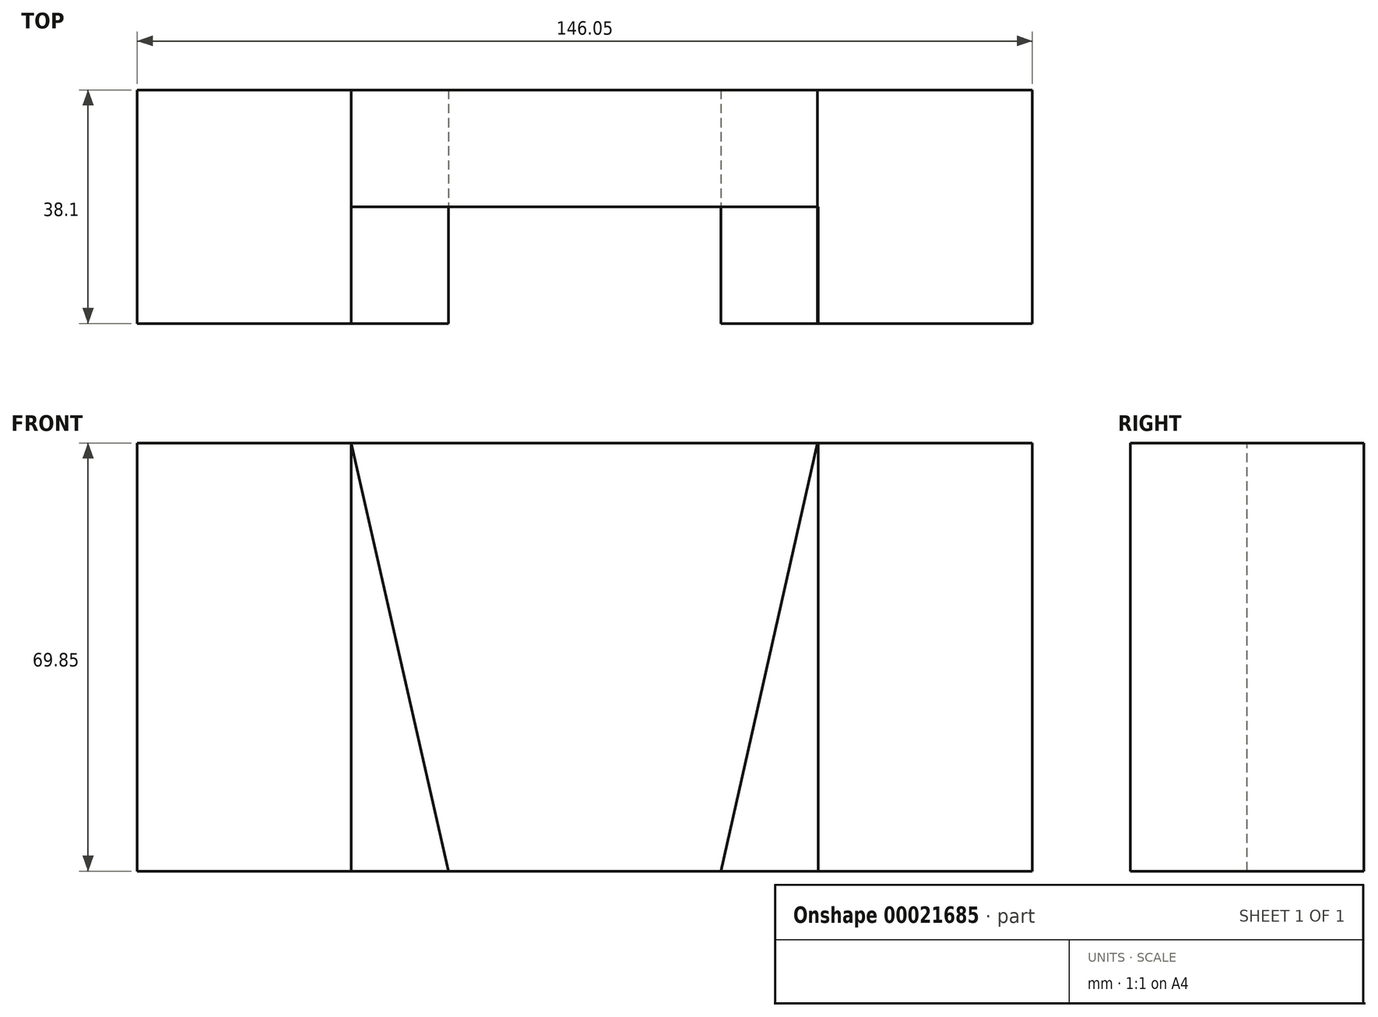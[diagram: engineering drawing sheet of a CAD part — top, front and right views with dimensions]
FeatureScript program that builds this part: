
annotation { "Feature Type Name" : "Feature", "Feature Type Description" : "" }
export const myFeature = defineFeature(function(context is Context, id is Id, definition is map)
    precondition{}
    {
        {
            var Q0;
            Q0=qCreatedBy(makeId("Top.planeOp"),FACE);
            var sketch = newSketch(context, id + "F0", { "sketchPlane" : qUnion([Q0])});
            skLineSegment(sketch, "E0", {"start": v(-74.2, 38.1) * mm, "end": v(71.85, 38.1) * mm});
            skLineSegment(sketch, "E1", {"start": v(-74.2, 38.1) * mm, "end": v(-74.2, 0) * mm});
            skLineSegment(sketch, "E2", {"start": v(71.85, 38.1) * mm, "end": v(36.92, 38.1) * mm});
            skLineSegment(sketch, "E3", {"start": v(36.92, 38.1) * mm, "end": v(-39.28, 38.1) * mm});
            skLineSegment(sketch, "E4", {"start": v(-74.2, 0) * mm, "end": v(-39.28, 0) * mm});
            skLineSegment(sketch, "E5", {"start": v(-39.28, 0) * mm, "end": v(-39.28, 19.05) * mm});
            skLineSegment(sketch, "E6", {"start": v(-39.28, 19.05) * mm, "end": v(36.92, 19.05) * mm});
            skLineSegment(sketch, "E7", {"start": v(36.92, 19.05) * mm, "end": v(36.92, 0) * mm});
            skLineSegment(sketch, "E8", {"start": v(36.92, 0) * mm, "end": v(71.85, 0) * mm});
            skLineSegment(sketch, "E9", {"start": v(71.85, 0) * mm, "end": v(71.85, 38.1) * mm});
            skSolve(sketch);
        }
        {
            var Q0;
            Q0=qCreatedBy(makeId("Front.planeOp"),FACE);
            var sketch = newSketch(context, id + "F1", { "sketchPlane" : qUnion([Q0])});
            skLineSegment(sketch, "E10", {"start": v(-74.2, 0) * mm, "end": v(-74.2, -69.85) * mm});
            skLineSegment(sketch, "E11", {"start": v(-74.2, -69.85) * mm, "end": v(-23.4, -69.85) * mm});
            skLineSegment(sketch, "E12", {"start": v(-23.4, -69.85) * mm, "end": v(-39.28, 0) * mm});
            skLineSegment(sketch, "E13", {"start": v(71.85, 0) * mm, "end": v(71.85, -69.85) * mm});
            skLineSegment(sketch, "E14", {"start": v(71.85, -69.85) * mm, "end": v(21.05, -69.85) * mm});
            skLineSegment(sketch, "E15", {"start": v(21.05, -69.85) * mm, "end": v(36.8, 0) * mm});
            skLineSegment(sketch, "E16", {"start": v(-74.2, 0) * mm, "end": v(-39.28, 0) * mm});
            skLineSegment(sketch, "E17", {"start": v(36.8, 0) * mm, "end": v(71.85, 0) * mm});
            skSolve(sketch);
        }
        {
            var Q0;
            Q0=makeQuery(id+"F1.imprint","IMPRINT",FACE,{"disambiguationData":[TD([[makeQuery(id+"F1.imprint","IMPRINT",EDGE,{"derivedFrom":sQuery(id+"F1.wireOp",EDGE,"E10")}),1.0]])]});
            var Q1;
            Q1=makeQuery(id+"F1.imprint","IMPRINT",FACE,{"disambiguationData":[TD([[makeQuery(id+"F1.imprint","IMPRINT",EDGE,{"derivedFrom":sQuery(id+"F1.wireOp",EDGE,"E13")}),-1.0]])]});
            extrude(context, id + "F2", {"entities" : qUnion([Q0, Q1]), "oppositeDirection" : true, "depth" : 38.1 * mm});
        }
        {
            var Q0;
            Q0=makeQuery(id+"F0.imprint","IMPRINT",FACE,{"disambiguationData":[TD([[makeQuery(id+"F0.imprint","IMPRINT",EDGE,{"derivedFrom":sQuery(id+"F0.wireOp",EDGE,"E0")}),-1.0]])]});
            extrude(context, id + "F3", {"entities" : qUnion([Q0]), "oppositeDirection" : true, "depth" : 69.85 * mm});
        }
    });
